# Revit family: Shower-Handshower_Kit-KOHLER-ACCLIV-K-33081T_1
name_source: partatom
category: Plumbing Fixtures
units: mm (PartAtom-declared; Revit-internal decimal feet)

## family parameters
Cut with Voids When Loaded = No
Host = Face
OmniClass Number = 23.31.17.00
OmniClass Title = Showers
Part Type = Normal
Room Calculation Point = No
Round Connector Dimension = Use Diameter
Shared = No

## types (4) — shared parameters
ADA Compliant = No
Assembly Code = D2010700
CW Connection = Yes
Cold Water Inlet = Cold Water Inlet
Date Modified = 16/11/2022
Default Elevation = 36"
Description = Exposed bath and shower faucet - spoon OL
Drain Included = No
Flow Rate = 0 GPM
HW Connection = Yes
Handle Clearance = 6 1/2"
Height = 5 3/16"
Hot Water Inlet = Hot Water Inlet
Length = 6 3/4"
Manufacturer = KOHLER Co.
Master Format 2014 = 22 42 23
Master Format 2014 Name = Residential Showers
Material = Premium Metal Construction
Panel Thickness = 4 5/16"
Pressure = 0.00 psi
Product Name = ACCLIV
Spout Reach = 6 3/4"
URL = http://www.kohler.com.cn
Vent Connection = No
Waste Connection = No
Waste Water Outlet = Waste Water Outlet
WaterSense Certified = No
Width = 5 7/8"

## per-type parameters (varying)
| type | Finish | Model | Secondary Finish | Type |
| CP-Polished Chrome | Kohler-Metal-CP-Polished_Chrome | K-33081T-4-CP | Kohler-Plastic-0-White | 1 |
| BN-Roman Silver | Kohler-Metal-BN-Roman_Silver | K-33081T-4-BN | Kohler-Plastic-0-White | 2 |
| AF-Flange Gold | Kohler-Metal-AF-Flange_Gold | K-33081T-4-AF | Kohler-Plastic-0-White | 3 |
| BL-Matte Black | Kohler-Metal-BL-Matte_Black | K-33081T-4-BL | Kohler-Plastic-58-Thunder_Grey | 4 |

## geometry (parser evidence)
native form markers: Sweep x5
no freeform markers — native parametric forms only
